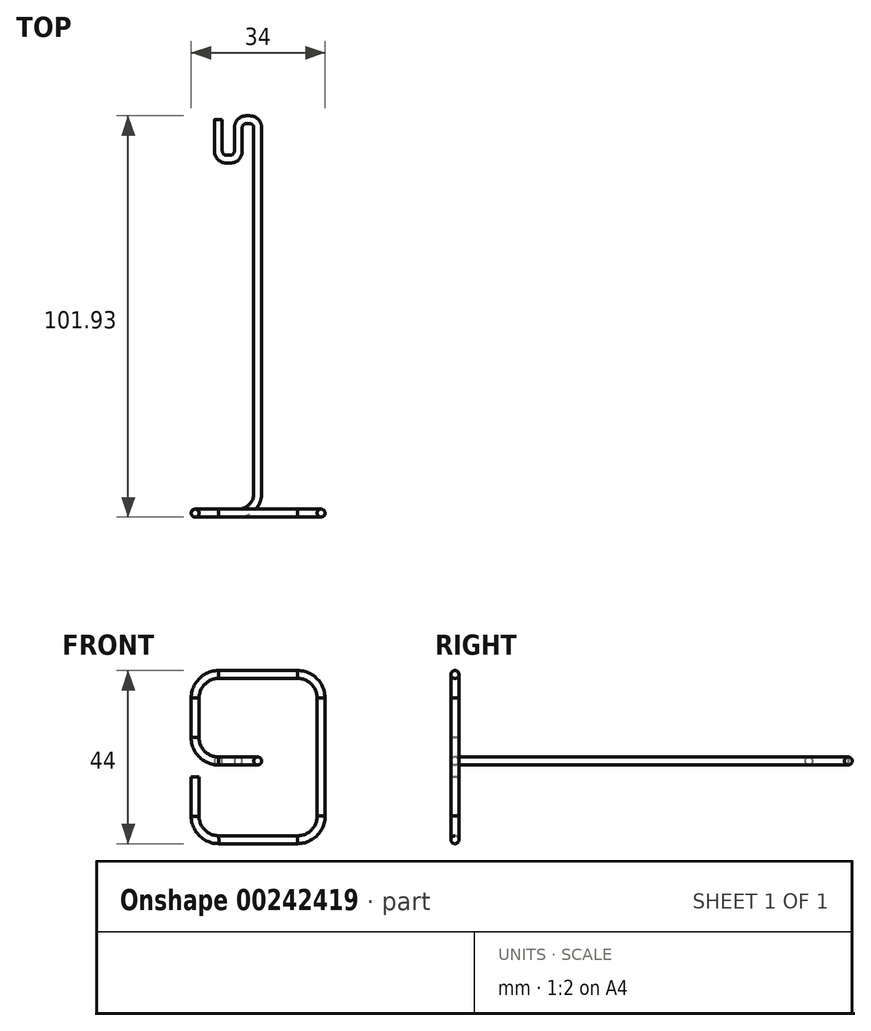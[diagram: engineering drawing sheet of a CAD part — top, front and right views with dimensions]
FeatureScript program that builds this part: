
annotation { "Feature Type Name" : "Feature", "Feature Type Description" : "" }
export const myFeature = defineFeature(function(context is Context, id is Id, definition is map)
    precondition{}
    {
        {
            var Q0;
            Q0=qCreatedBy(makeId("Top.planeOp"),FACE);
            var sketch = newSketch(context, id + "F0", { "sketchPlane" : qUnion([Q0])});
            skLineSegment(sketch, "E0", {"start": v(-10, 32.45) * mm, "end": v(-10, 24.45) * mm});
            skLineSegment(sketch, "E1", {"start": v(-8, 22.45) * mm, "end": v(-7, 22.45) * mm});
            skLineSegment(sketch, "E2", {"start": v(-5, 24.45) * mm, "end": v(-5, 30.45) * mm});
            skLineSegment(sketch, "E3", {"start": v(-3, 32.45) * mm, "end": v(-2, 32.45) * mm});
            skLineSegment(sketch, "E4", {"start": v(0, 30.45) * mm, "end": v(0, -62.55) * mm});
            skPoint(sketch, "E5.visualSharp", {"position": v(-10, 22.45) * mm});
            skArc(sketch, "E5.filletArc", {"start": v(-10, 24.45) * mm, "mid": v(-9.41, 23.04) * mm, "end": v(-8, 22.45) * mm});
            skPoint(sketch, "E6.visualSharp", {"position": v(-5, 22.45) * mm});
            skArc(sketch, "E6.filletArc", {"start": v(-7, 22.45) * mm, "mid": v(-5.59, 23.04) * mm, "end": v(-5, 24.45) * mm});
            skPoint(sketch, "E7.visualSharp", {"position": v(-5, 32.45) * mm});
            skArc(sketch, "E7.filletArc", {"start": v(-3, 32.45) * mm, "mid": v(-4.41, 31.87) * mm, "end": v(-5, 30.45) * mm});
            skPoint(sketch, "E8.visualSharp", {"position": v(0, 32.45) * mm});
            skArc(sketch, "E8.filletArc", {"start": v(0, 30.45) * mm, "mid": v(-0.59, 31.87) * mm, "end": v(-2, 32.45) * mm});
            skLineSegment(sketch, "E9", {"start": v(-5, -67.55) * mm, "end": v(-10, -67.55) * mm});
            skPoint(sketch, "E10.visualSharp", {"position": v(0, -67.55) * mm});
            skArc(sketch, "E10.filletArc", {"start": v(-5, -67.55) * mm, "mid": v(-1.46, -66.08) * mm, "end": v(0, -62.55) * mm});
            skSolve(sketch);
        }
        {
            var Q0;
            Q0=sQuery(id+"F0.wireOp",EDGE,"E3");
            var Q1;
            Q1=qCreatedBy(makeId("Top.planeOp"),FACE);
            cPlane(context, id + "F1", {"entities" : qUnion([Q0, Q1]), "cplaneType" : CPlaneType.LINE_ANGLE, "offset" : 25 * mm, "angle" : 90 * degree, "width" : 150 * mm, "height" : 150 * mm});
        }
        {
            var Q0;
            Q0=qCreatedBy(id+"F1.planeOp",FACE);
            var sketch = newSketch(context, id + "F2", { "sketchPlane" : qUnion([Q0])});
            skPoint(sketch, "E11.first.point", {"position": v(11.98, 0.03) * mm});
            skPoint(sketch, "E11.second.point", {"position": v(10, 0) * mm});
            skCircle(sketch, "E12", {"center": v(10.04, -1) * mm, "radius": 1 * mm});
            skPoint(sketch, "E12.first.point", {"position": v(11, -1.23) * mm});
            skPoint(sketch, "E12.second.point", {"position": v(9.09, -0.68) * mm});
            skSolve(sketch);
        }
        {
            var Q0;
            Q0 = qSketchRegion(id + "F2", true);
            var Q1;
            Q1=sQuery(id+"F0.wireOp",EDGE,"E0");
            var Q2;
            Q2=sQuery(id+"F0.wireOp",EDGE,"E5.filletArc");
            var Q3;
            Q3=sQuery(id+"F0.wireOp",EDGE,"E1");
            var Q4;
            Q4=sQuery(id+"F0.wireOp",EDGE,"E6.filletArc");
            var Q5;
            Q5=sQuery(id+"F0.wireOp",EDGE,"E2");
            var Q6;
            Q6=sQuery(id+"F0.wireOp",EDGE,"E7.filletArc");
            var Q7;
            Q7=sQuery(id+"F0.wireOp",EDGE,"E3");
            var Q8;
            Q8=sQuery(id+"F0.wireOp",EDGE,"E8.filletArc");
            var Q9;
            Q9=sQuery(id+"F0.wireOp",EDGE,"E4");
            var Q10;
            Q10=sQuery(id+"F0.wireOp",EDGE,"E10.filletArc");
            sweep(context, id + "F3", {"profiles" : qUnion([Q0]), "path" : qUnion([Q1, Q2, Q3, Q4, Q5, Q6, Q7, Q8, Q9, Q10])});
        }
        {
            var Q0;
            Q0=sQuery(id+"F0.wireOp",EDGE,"E9");
            cPlane(context, id + "F4", {"entities" : qUnion([Q0]), "cplaneType" : CPlaneType.LINE_ANGLE, "offset" : 25 * mm, "angle" : 0 * degree, "width" : 150 * mm, "height" : 150 * mm});
        }
        {
            var Q0;
            Q0=qCreatedBy(id+"F4.planeOp",FACE);
            var sketch = newSketch(context, id + "F5", { "sketchPlane" : qUnion([Q0])});
            skLineSegment(sketch, "E13", {"start": v(-14.93, 5) * mm, "end": v(-14.93, 15) * mm});
            skLineSegment(sketch, "E14", {"start": v(-9.93, 20) * mm, "end": v(10.07, 20) * mm});
            skLineSegment(sketch, "E15", {"start": v(15.07, 15) * mm, "end": v(15.07, -15) * mm});
            skLineSegment(sketch, "E16", {"start": v(-14.93, -15) * mm, "end": v(-14.93, -5) * mm});
            skLineSegment(sketch, "E17", {"start": v(10.07, -20) * mm, "end": v(-9.93, -20) * mm});
            skPoint(sketch, "E18.visualSharp", {"position": v(-14.93, 20) * mm});
            skArc(sketch, "E18.filletArc", {"start": v(-9.93, 20) * mm, "mid": v(-13.47, 18.54) * mm, "end": v(-14.93, 15) * mm});
            skPoint(sketch, "E19.visualSharp", {"position": v(15.07, 20) * mm});
            skArc(sketch, "E19.filletArc", {"start": v(15.07, 15) * mm, "mid": v(13.6, 18.54) * mm, "end": v(10.07, 20) * mm});
            skPoint(sketch, "E20.visualSharp", {"position": v(15.07, -20) * mm});
            skArc(sketch, "E20.filletArc", {"start": v(10.07, -20) * mm, "mid": v(13.6, -18.54) * mm, "end": v(15.07, -15) * mm});
            skPoint(sketch, "E21.visualSharp", {"position": v(-14.93, -20) * mm});
            skArc(sketch, "E21.filletArc", {"start": v(-14.93, -15) * mm, "mid": v(-13.47, -18.54) * mm, "end": v(-9.93, -20) * mm});
            skLineSegment(sketch, "E22", {"start": v(-9.93, 0) * mm, "end": v(-9.61, 0) * mm});
            skPoint(sketch, "E23.visualSharp", {"position": v(-14.93, 0) * mm});
            skArc(sketch, "E23.filletArc", {"start": v(-14.93, 5) * mm, "mid": v(-13.47, 1.46) * mm, "end": v(-9.93, 0) * mm});
            skSolve(sketch);
        }
        {
            var Q0;
            Q0=makeQuery(id+"F3.opSweep","CAP_FACE",FACE,{"disambiguationData":[OSD([sQuery(id+"F0.wireOp",VERTEX,"E10.filletArc.start"),sQuery(id+"F2.wireOp",EDGE,"E12")])],"isStart":false});
            var Q1;
            Q1=sQuery(id+"F0.wireOp",EDGE,"E9");
            sweep(context, id + "F6", {"operationType" : NewBodyOperationType.ADD, "profiles" : qUnion([Q0]), "path" : qUnion([Q1])});
        }
        {
            var Q0;
            Q0=makeQuery(id+"F6.opSweep","CAP_FACE",FACE,{"disambiguationData":[OSD([sQuery(id+"F0.wireOp",VERTEX,"E9.end"),sQuery(id+"F0.wireOp",VERTEX,"E10.filletArc.start"),sQuery(id+"F2.wireOp",EDGE,"E12")])],"isStart":false});
            var Q1;
            Q1 = qConstructionFilter(qBodyType(qCreatedBy(id + "F5" ,EDGE), BodyType.WIRE), ConstructionObject.NO);
            sweep(context, id + "F7", {"operationType" : NewBodyOperationType.ADD, "profiles" : qUnion([Q0]), "path" : qUnion([Q1])});
        }
    });
